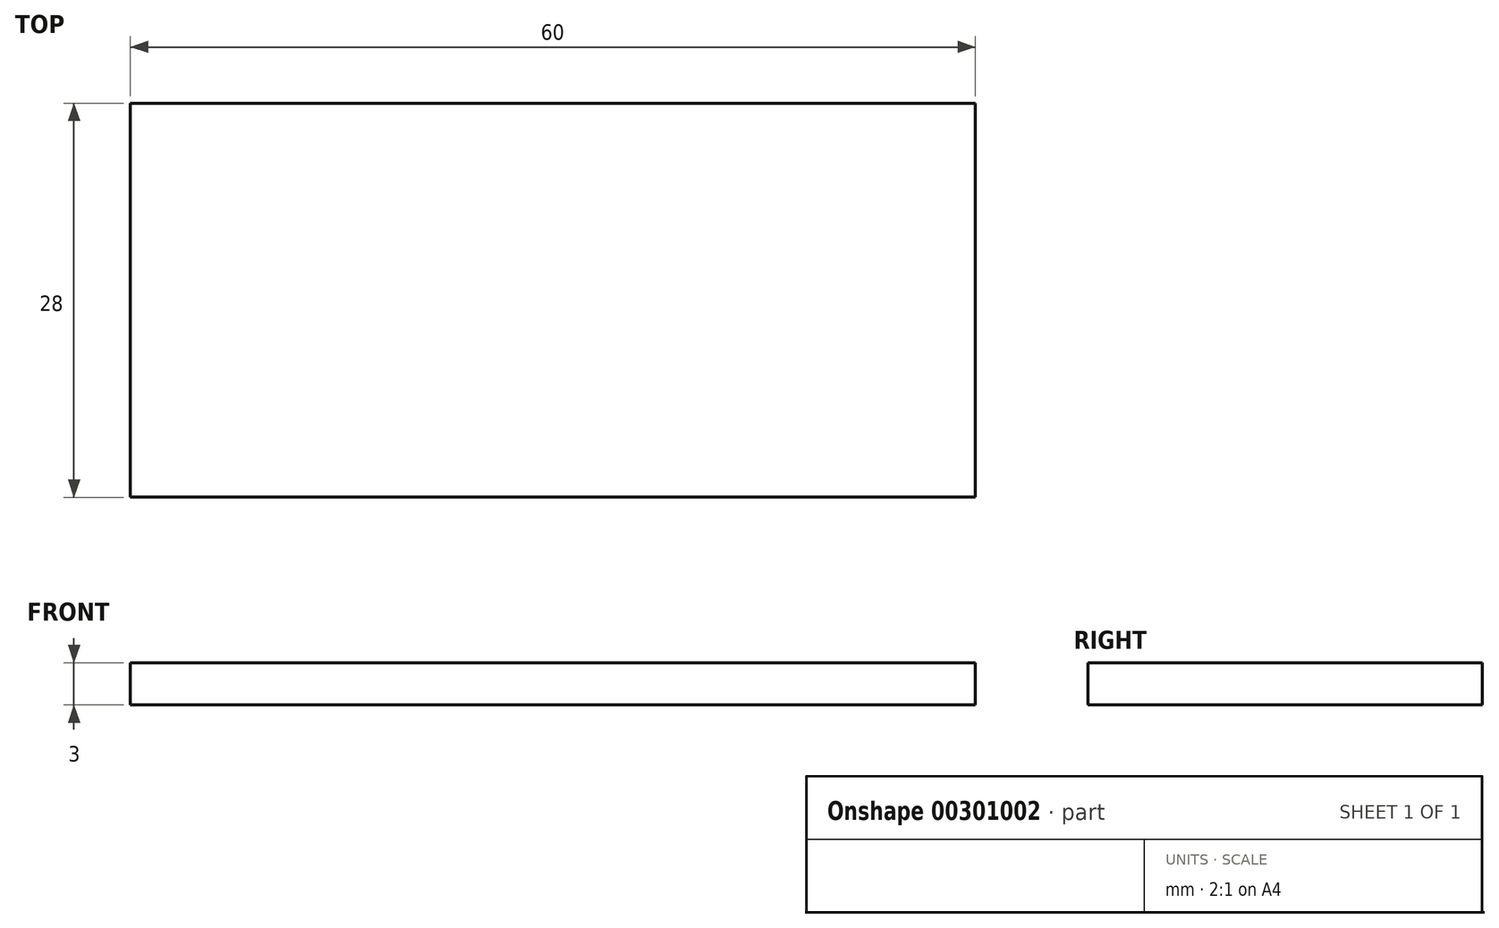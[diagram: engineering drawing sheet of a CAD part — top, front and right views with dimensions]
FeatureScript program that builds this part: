
annotation { "Feature Type Name" : "Feature", "Feature Type Description" : "" }
export const myFeature = defineFeature(function(context is Context, id is Id, definition is map)
    precondition{}
    {
        {
            var Q0;
            Q0=qCreatedBy(makeId("Top.planeOp"),FACE);
            var sketch = newSketch(context, id + "F0", { "sketchPlane" : qUnion([Q0])});
            skLineSegment(sketch, "E0", {"start": v(-31.3, 14.93) * mm, "end": v(-31.3, -13.07) * mm});
            skLineSegment(sketch, "E1", {"start": v(-31.3, -13.07) * mm, "end": v(28.7, -13.07) * mm});
            skLineSegment(sketch, "E2", {"start": v(28.7, -13.07) * mm, "end": v(28.7, 14.93) * mm});
            skLineSegment(sketch, "E3", {"start": v(28.7, 14.93) * mm, "end": v(-31.3, 14.93) * mm});
            skSolve(sketch);
        }
        {
            var Q0;
            Q0=makeQuery(id+"F0.imprint","IMPRINT",FACE,{"disambiguationData":[TD([[makeQuery(id+"F0.imprint","IMPRINT",EDGE,{"derivedFrom":sQuery(id+"F0.wireOp",EDGE,"E0")}),1.0]])]});
            extrude(context, id + "F1", {"entities" : qUnion([Q0]), "depth" : 3 * mm, "offsetDistance" : 25 * mm});
        }
    });
